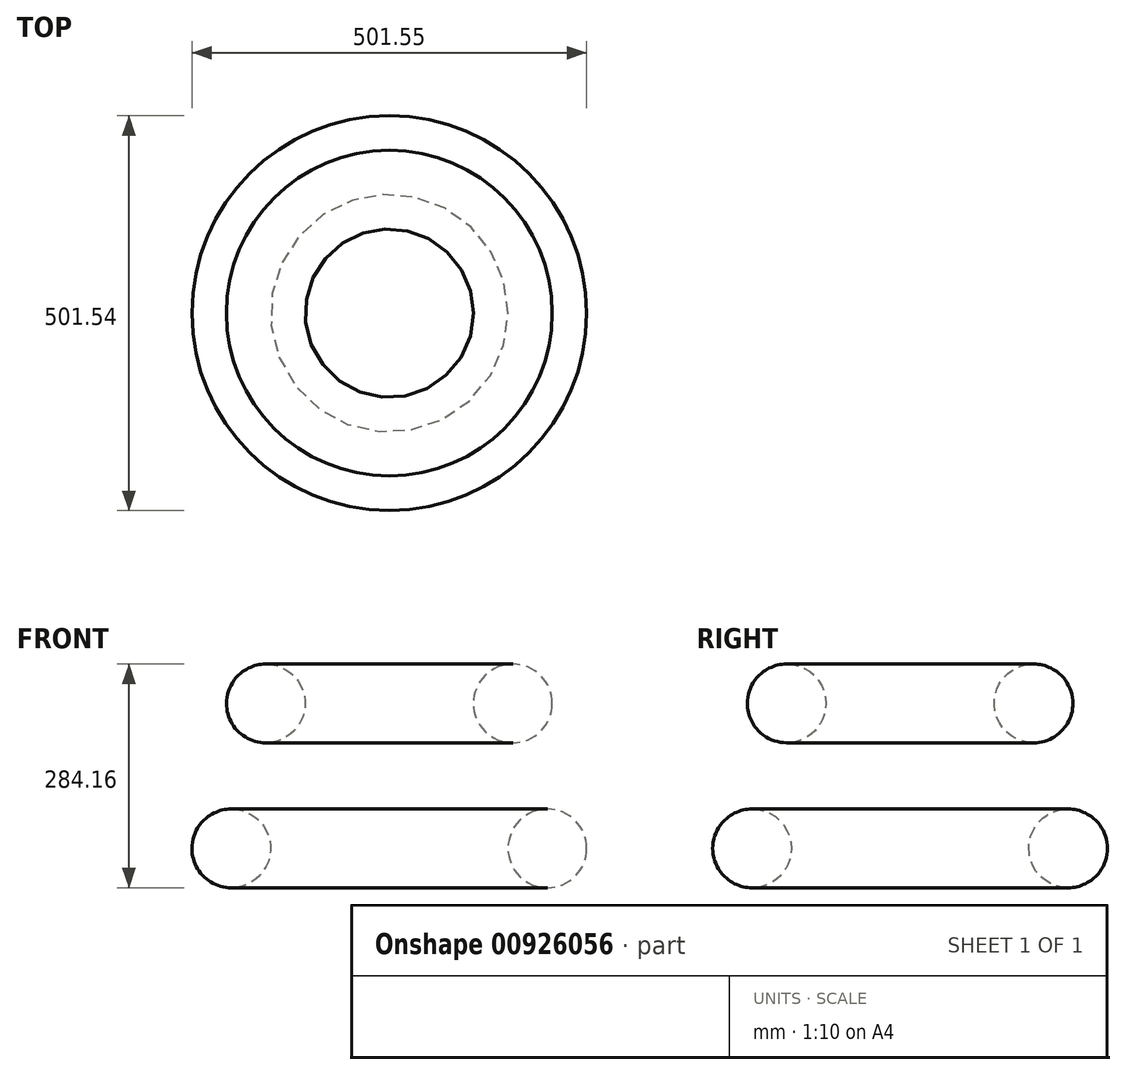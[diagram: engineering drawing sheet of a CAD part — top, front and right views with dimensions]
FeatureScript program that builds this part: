
annotation { "Feature Type Name" : "Feature", "Feature Type Description" : "" }
export const myFeature = defineFeature(function(context is Context, id is Id, definition is map)
    precondition{}
    {
        {
            var Q0;
            Q0=qCreatedBy(makeId("Front.planeOp"),FACE);
            var sketch = newSketch(context, id + "F0", { "sketchPlane" : qUnion([Q0])});
            skCircle(sketch, "E0", {"center": v(-50, 0) * mm, "radius": 50 * mm});
            skCircle(sketch, "E1", {"center": v(307.64, 184.16) * mm, "radius": 50 * mm});
            skLineSegment(sketch, "E2", {"start": v(150.77, 60.11) * mm, "end": v(150.77, -84.55) * mm});
            skSolve(sketch);
        }
        {
            var Q0;
            Q0=makeQuery(id+"F0.imprint","IMPRINT",FACE,{"disambiguationData":[TD([[makeQuery(id+"F0.imprint","IMPRINT",EDGE,{"derivedFrom":sQuery(id+"F0.wireOp",EDGE,"E0")}),1.0]])]});
            var Q1;
            Q1=makeQuery(id+"F0.imprint","IMPRINT",FACE,{"disambiguationData":[TD([[makeQuery(id+"F0.imprint","IMPRINT",EDGE,{"derivedFrom":sQuery(id+"F0.wireOp",EDGE,"E1")}),1.0]])]});
            var Q2;
            Q2=sQuery(id+"F0.wireOp",EDGE,"E2");
            revolve(context, id + "F1", {"surfaceOperationType" : NewSurfaceOperationType.NEW, "entities" : qUnion([Q0, Q1]), "axis" : qUnion([Q2]), "revolveType" : RevolveType.FULL});
        }
    });
